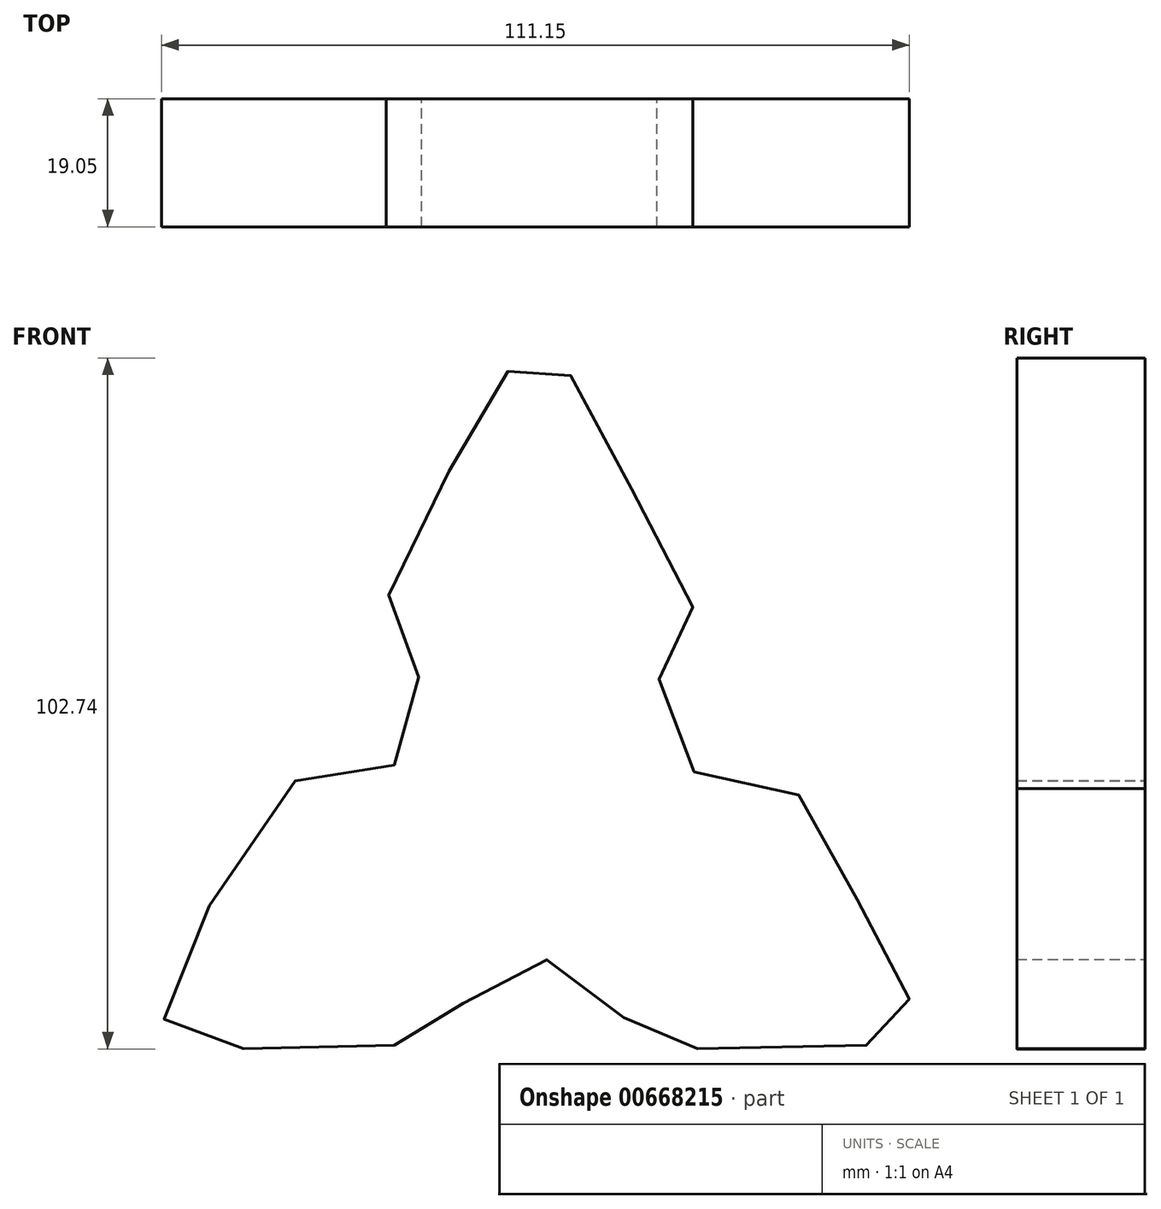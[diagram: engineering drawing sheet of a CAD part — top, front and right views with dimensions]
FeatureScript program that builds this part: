
annotation { "Feature Type Name" : "Feature", "Feature Type Description" : "" }
export const myFeature = defineFeature(function(context is Context, id is Id, definition is map)
    precondition{}
    {
        {
            var Q0;
            Q0=qCreatedBy(makeId("Front.planeOp"),FACE);
            var sketch = newSketch(context, id + "F0", { "sketchPlane" : qUnion([Q0])});
            skFitSpline(sketch, "E0", {"points": [v(-17.57, 32.99) * mm, v(-12.49, 42.15) * mm, v(-8.85, 47.82) * mm, v(-5.94, 49.56) * mm, v(-3.04, 49.7) * mm, v(0, 47.82) * mm, v(2.34, 44.47) * mm, v(8.16, 32.99) * mm, v(17.17, 16.85) * mm, v(18.63, 13.07) * mm, v(18.48, 10.46) * mm, v(16.3, 6.82) * mm, v(13.68, 2.17) * mm, v(13.68, -3.8) * mm, v(16.88, -10.33) * mm, v(27.78, -14.11) * mm, v(33.02, -14.4) * mm, v(35.34, -16) * mm, v(36.5, -18.76) * mm, v(44.97, -33.75) * mm, v(49.67, -42.23) * mm, v(50.85, -45.29) * mm, v(50.14, -48.58) * mm, v(48.26, -50.93) * mm, v(45.9, -52.11) * mm, v(39.55, -52.58) * mm, v(16.49, -52.82) * mm, v(11.3, -51.88) * mm, v(9.43, -50) * mm, v(7.78, -47.17) * mm, v(3.78, -42.46) * mm, v(-2.81, -39.64) * mm, v(-8.93, -40.58) * mm, v(-14.11, -43.64) * mm, v(-17.64, -50.7) * mm, v(-20.7, -52.11) * mm, v(-26.12, -52.35) * mm, v(-40, -52.58) * mm, v(-54.12, -52.82) * mm, v(-58.13, -51.64) * mm, v(-59.77, -48.82) * mm, v(-60.24, -46) * mm, v(-56.24, -37.52) * mm, v(-44.24, -15.4) * mm, v(-40.47, -13.04) * mm, v(-34.12, -13.04) * mm, v(-27.06, -11.63) * mm, v(-23.06, -7.4) * mm, v(-21.64, -2.45) * mm, v(-22.82, 4.61) * mm, v(-26.12, 10.03) * mm, v(-26.82, 13.32) * mm, v(-24.23, 19.68) * mm, v(-17.57, 32.99) * mm]});
            skSolve(sketch);
        }
        {
            var Q0;
            Q0=makeQuery(id+"F0.imprint","IMPRINT",FACE,{"disambiguationData":[TD([[makeQuery(id+"F0.imprint","IMPRINT",EDGE,{"derivedFrom":sQuery(id+"F0.wireOp",EDGE,"E0")}),-1.0]])]});
            extrude(context, id + "F1", {"entities" : qUnion([Q0]), "depth" : 19.05 * mm, "offsetDistance" : 25.4 * mm});
        }
    });
